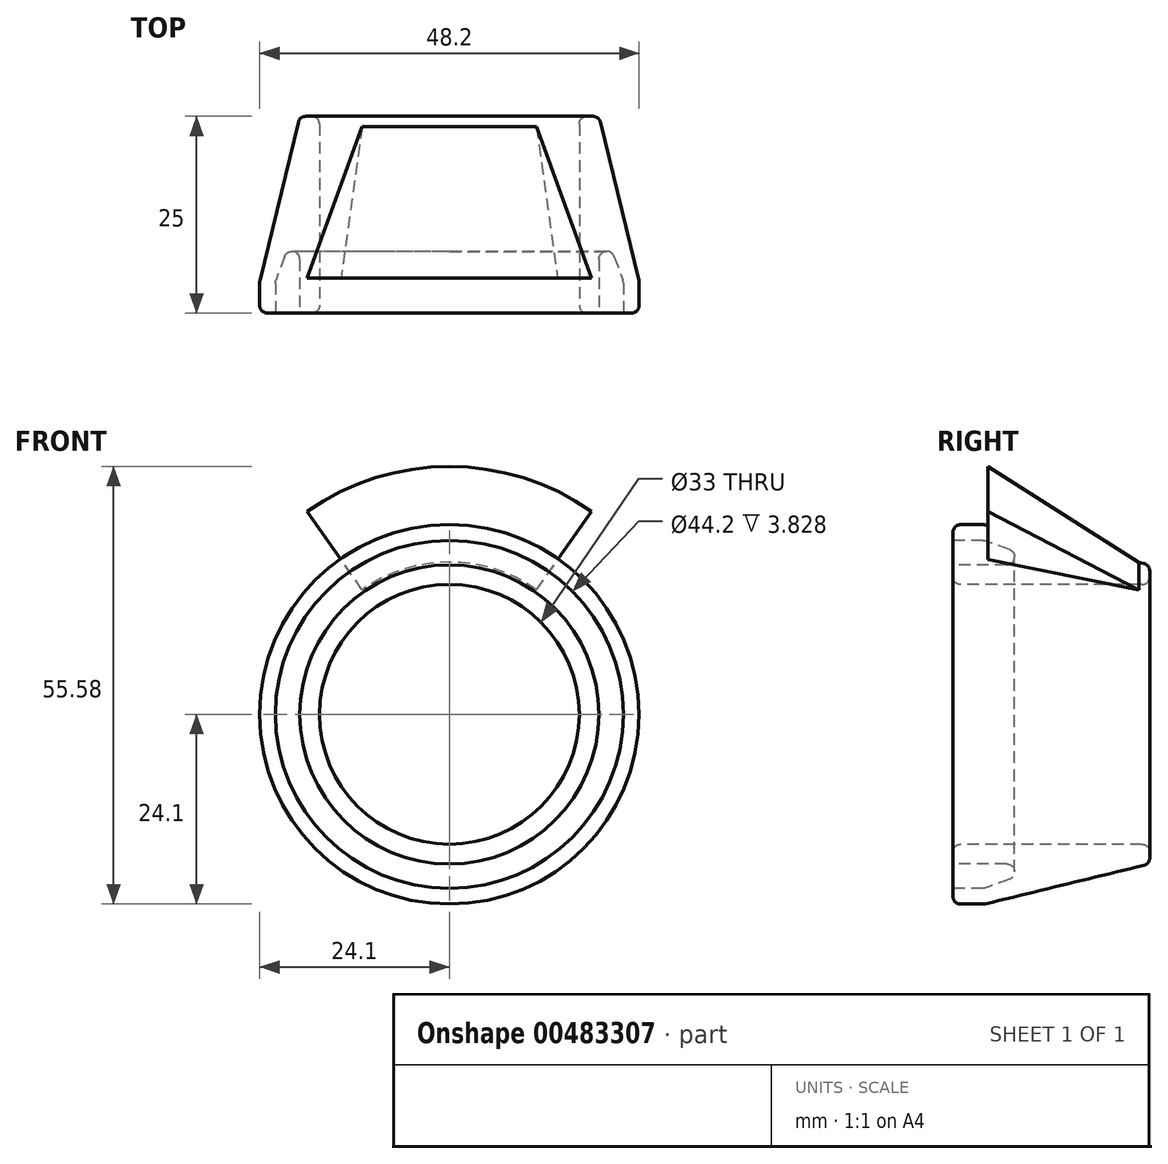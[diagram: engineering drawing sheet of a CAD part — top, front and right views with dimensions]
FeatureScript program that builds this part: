
annotation { "Feature Type Name" : "Feature", "Feature Type Description" : "" }
export const myFeature = defineFeature(function(context is Context, id is Id, definition is map)
    precondition{}
    {
        {
            var Q0;
            Q0=qCreatedBy(makeId("Right.planeOp"),FACE);
            var sketch = newSketch(context, id + "F0", { "sketchPlane" : qUnion([Q0])});
            skLineSegment(sketch, "E0", {"start": v(0.97, 16.5) * mm, "end": v(24.03, 16.5) * mm});
            skLineSegment(sketch, "E1", {"start": v(25, 17.47) * mm, "end": v(25, 18.23) * mm});
            skLineSegment(sketch, "E2", {"start": v(24.26, 19.18) * mm, "end": v(4.11, 24.07) * mm});
            skLineSegment(sketch, "E3", {"start": v(3.88, 24.1) * mm, "end": v(0.97, 24.1) * mm});
            skLineSegment(sketch, "E4", {"start": v(0, 23.13) * mm, "end": v(0, 22.1) * mm});
            skLineSegment(sketch, "E5", {"start": v(0, 22.1) * mm, "end": v(3.83, 22.1) * mm});
            skLineSegment(sketch, "E6", {"start": v(4.16, 22.04) * mm, "end": v(7.18, 20.94) * mm});
            skPoint(sketch, "E6.endSnap0", {"position": v(12.5, 16.5) * mm});
            skLineSegment(sketch, "E7", {"start": v(6.84, 19) * mm, "end": v(0, 19) * mm});
            skLineSegment(sketch, "E8", {"start": v(0, 19) * mm, "end": v(0, 17.47) * mm});
            skPoint(sketch, "E9.visualSharp", {"position": v(12.5, 19) * mm});
            skArc(sketch, "E9.filletArc", {"start": v(6.84, 19) * mm, "mid": v(7.82, 19.83) * mm, "end": v(7.18, 20.94) * mm});
            skPoint(sketch, "E10.visualSharp", {"position": v(25, 16.5) * mm});
            skArc(sketch, "E10.filletArc", {"start": v(24.03, 16.5) * mm, "mid": v(24.71, 16.79) * mm, "end": v(25, 17.47) * mm});
            skPoint(sketch, "E11.visualSharp", {"position": v(25, 19) * mm});
            skArc(sketch, "E11.filletArc", {"start": v(25, 18.23) * mm, "mid": v(24.8, 18.84) * mm, "end": v(24.26, 19.18) * mm});
            skPoint(sketch, "E12.visualSharp", {"position": v(0, 16.5) * mm});
            skArc(sketch, "E12.filletArc", {"start": v(0, 17.47) * mm, "mid": v(0.29, 16.79) * mm, "end": v(0.97, 16.5) * mm});
            skPoint(sketch, "E13.visualSharp", {"position": v(0, 24.1) * mm});
            skArc(sketch, "E13.filletArc", {"start": v(0.97, 24.1) * mm, "mid": v(0.29, 23.81) * mm, "end": v(0, 23.13) * mm});
            skPoint(sketch, "E14.visualSharp", {"position": v(4, 24.1) * mm});
            skArc(sketch, "E14.filletArc", {"start": v(4.11, 24.07) * mm, "mid": v(4, 24.1) * mm, "end": v(3.88, 24.1) * mm});
            skPoint(sketch, "E15.visualSharp", {"position": v(4, 22.1) * mm});
            skArc(sketch, "E15.filletArc", {"start": v(4.16, 22.04) * mm, "mid": v(4, 22.09) * mm, "end": v(3.83, 22.1) * mm});
            skLineSegment(sketch, "E16", {"start": v(0, 0) * mm, "end": v(26.32, 0) * mm});
            skSolve(sketch);
        }
        {
            var Q0;
            Q0 = qSketchRegion(id + "F0", true);
            var Q1;
            Q1=sQuery(id+"F0.wireOp",EDGE,"E16");
            revolve(context, id + "F1", {"entities" : qUnion([Q0]), "axis" : qUnion([Q1]), "revolveType" : RevolveType.FULL});
        }
        {
            var Q0;
            Q0=qCreatedBy(makeId("Right.planeOp"),FACE);
            var sketch = newSketch(context, id + "F2", { "sketchPlane" : qUnion([Q0])});
            skLineSegment(sketch, "E17", {"start": v(24.22, 18.97) * mm, "end": v(4.44, 31.48) * mm});
            skLineSegment(sketch, "E18", {"start": v(4.44, 31.48) * mm, "end": v(4.44, 23.25) * mm});
            skLineSegment(sketch, "E19", {"start": v(4.44, 23.25) * mm, "end": v(24.22, 18.97) * mm});
            skLineSegment(sketch, "E20", {"start": v(0, 0) * mm, "end": v(28.93, 0) * mm});
            skSolve(sketch);
        }
        {
            var Q0;
            Q0 = qSketchRegion(id + "F2", true);
            var Q1;
            Q1=sQuery(id+"F2.wireOp",EDGE,"E20");
            revolve(context, id + "F3", {"operationType" : NewBodyOperationType.ADD, "entities" : qUnion([Q0]), "axis" : qUnion([Q1]), "revolveType" : RevolveType.TWO_DIRECTIONS, "angle" : 35 * degree, "angleBack" : 325 * degree});
        }
    });
